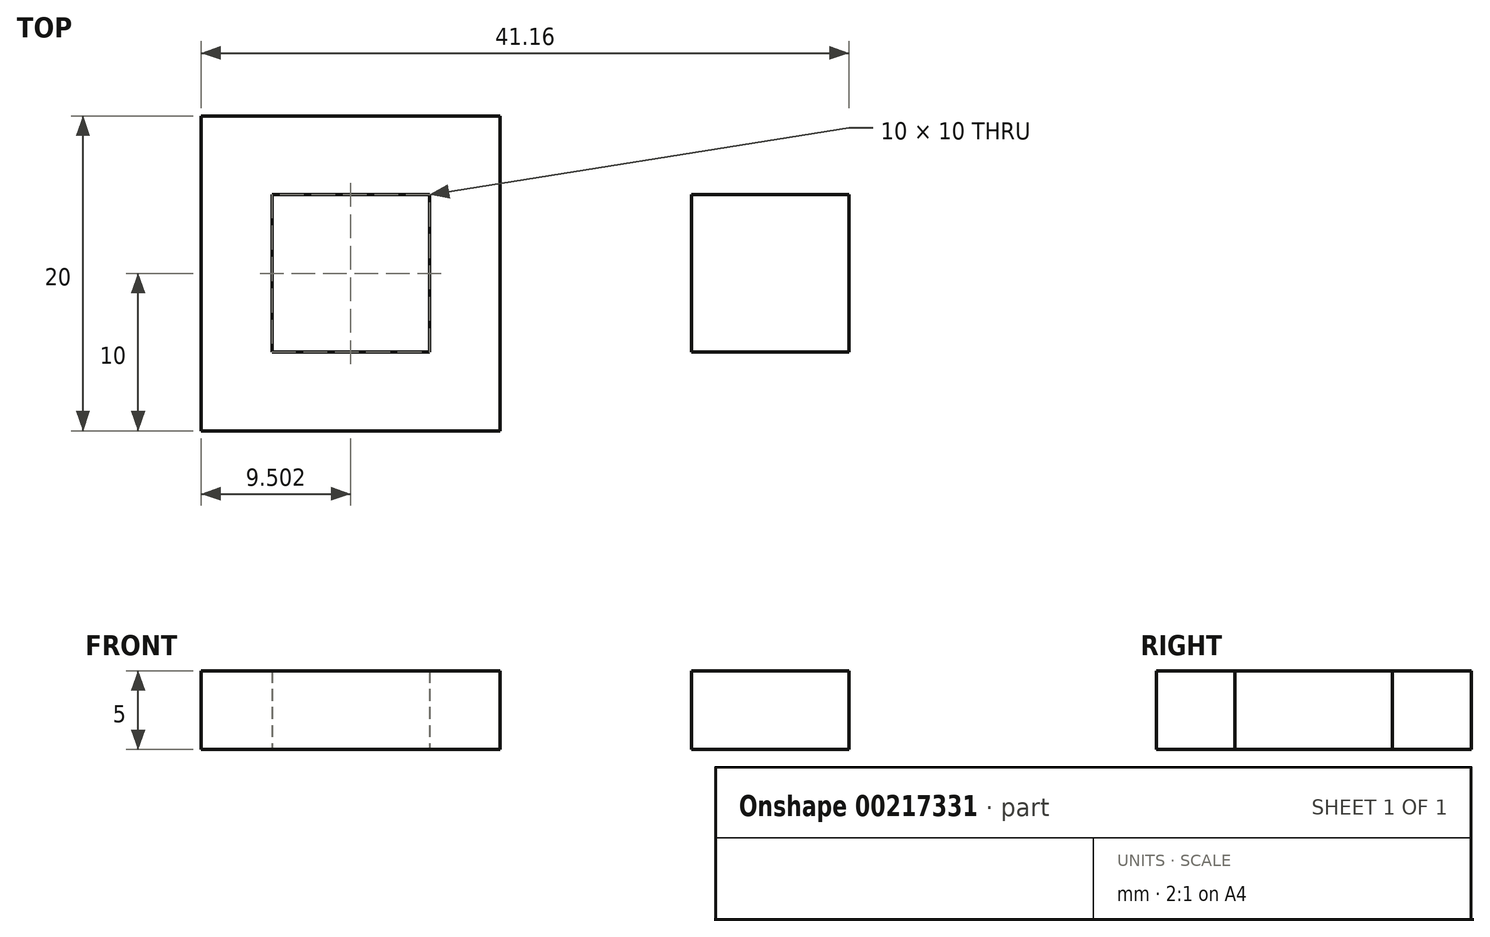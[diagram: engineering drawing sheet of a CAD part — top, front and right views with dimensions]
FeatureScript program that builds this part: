
annotation { "Feature Type Name" : "Feature", "Feature Type Description" : "" }
export const myFeature = defineFeature(function(context is Context, id is Id, definition is map)
    precondition{}
    {
        {
            var Q0;
            Q0=qCreatedBy(makeId("Top.planeOp"),FACE);
            var sketch = newSketch(context, id + "F0", { "sketchPlane" : qUnion([Q0])});
            skLineSegment(sketch, "E0.bottom", {"start": v(-8.3, 10) * mm, "end": v(-27.3, 10) * mm});
            skLineSegment(sketch, "E0.top", {"start": v(-8.3, -10) * mm, "end": v(-27.3, -10) * mm});
            skLineSegment(sketch, "E0.left", {"start": v(-8.3, 10) * mm, "end": v(-8.3, -10) * mm});
            skLineSegment(sketch, "E0.right", {"start": v(-27.3, 10) * mm, "end": v(-27.3, -10) * mm});
            skPoint(sketch, "E0.middle", {"position": v(-17.8, 0) * mm});
            skLineSegment(sketch, "E1.bottom", {"start": v(-12.8, 5) * mm, "end": v(-22.8, 5) * mm});
            skLineSegment(sketch, "E1.top", {"start": v(-12.8, -5) * mm, "end": v(-22.8, -5) * mm});
            skLineSegment(sketch, "E1.left", {"start": v(-12.8, 5) * mm, "end": v(-12.8, -5) * mm});
            skLineSegment(sketch, "E1.right", {"start": v(-22.8, 5) * mm, "end": v(-22.8, -5) * mm});
            skLineSegment(sketch, "E2.bottom", {"start": v(13.86, 5) * mm, "end": v(3.86, 5) * mm});
            skLineSegment(sketch, "E2.top", {"start": v(13.86, -5) * mm, "end": v(3.86, -5) * mm});
            skLineSegment(sketch, "E2.left", {"start": v(13.86, 5) * mm, "end": v(13.86, -5) * mm});
            skLineSegment(sketch, "E2.right", {"start": v(3.86, 5) * mm, "end": v(3.86, -5) * mm});
            skPoint(sketch, "E2.middle", {"position": v(8.86, 0) * mm});
            skSolve(sketch);
        }
        {
            var Q0;
            Q0 = qSketchRegion(id + "F0", true);
            extrude(context, id + "F1", {"entities" : qUnion([Q0]), "depth" : 5 * mm});
        }
    });
